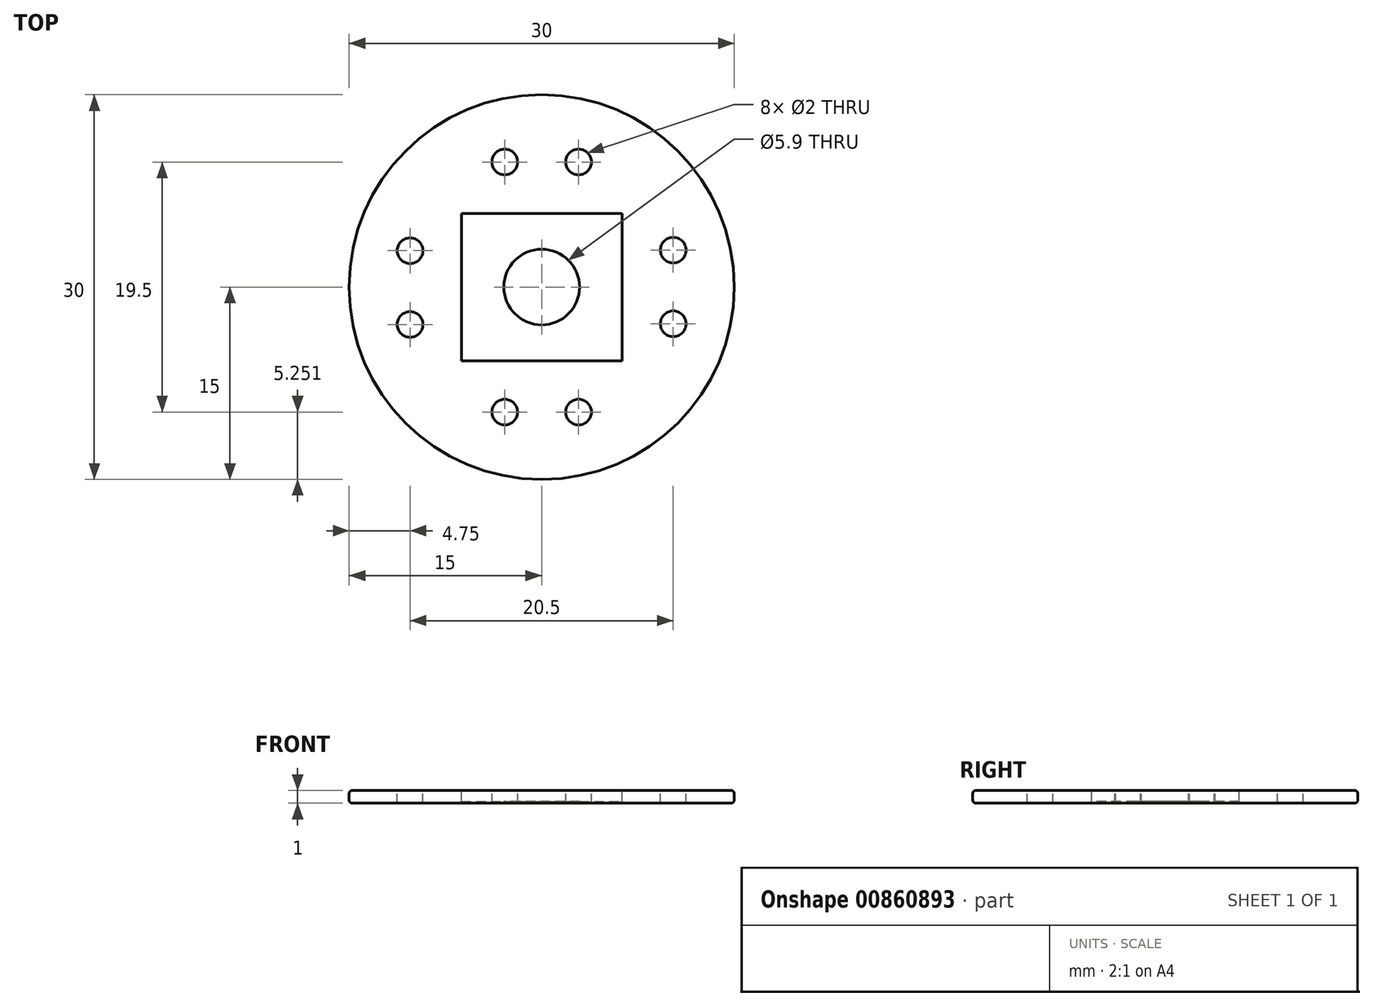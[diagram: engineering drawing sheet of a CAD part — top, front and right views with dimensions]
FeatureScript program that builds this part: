
annotation { "Feature Type Name" : "Feature", "Feature Type Description" : "" }
export const myFeature = defineFeature(function(context is Context, id is Id, definition is map)
    precondition{}
    {
        {
            var Q0;
            Q0=qCreatedBy(makeId("Top.planeOp"),FACE);
            var sketch = newSketch(context, id + "F0", { "sketchPlane" : qUnion([Q0])});
            skCircle(sketch, "E0", {"center": v(0, 0) * mm, "radius": 15 * mm});
            skSolve(sketch);
        }
        {
            var Q0;
            Q0=makeQuery(id+"F0.imprint","IMPRINT",FACE,{"disambiguationData":[TD([[makeQuery(id+"F0.imprint","IMPRINT",EDGE,{"derivedFrom":sQuery(id+"F0.wireOp",EDGE,"E0")}),1.0]])]});
            extrude(context, id + "F1", {"entities" : qUnion([Q0]), "depth" : 1 * mm, "offsetDistance" : 25 * mm});
        }
        {
            var Q0;
            Q0=makeQuery(id+"F1.opExtrude","CAP_FACE",FACE,{"disambiguationData":[OSD([sQuery(id+"F0.wireOp",EDGE,"E0")])],"isStart":false});
            var sketch = newSketch(context, id + "F2", { "sketchPlane" : qUnion([Q0])});
            skLineSegment(sketch, "E1.bottom", {"start": v(-6.25, 5.75) * mm, "end": v(6.25, 5.75) * mm});
            skLineSegment(sketch, "E1.top", {"start": v(-6.25, -5.75) * mm, "end": v(6.25, -5.75) * mm});
            skLineSegment(sketch, "E1.left", {"start": v(-6.25, 5.75) * mm, "end": v(-6.25, -5.75) * mm});
            skLineSegment(sketch, "E1.right", {"start": v(6.25, 5.75) * mm, "end": v(6.25, -5.75) * mm});
            skSolve(sketch);
        }
        {
            var Q0;
            Q0=makeQuery(id+"F2.imprint","IMPRINT",FACE,{"disambiguationData":[TD([[makeQuery(id+"F2.imprint","IMPRINT",EDGE,{"derivedFrom":sQuery(id+"F2.wireOp",EDGE,"E1.bottom")}),-1.0]])]});
            extrude(context, id + "F3", {"entities" : qUnion([Q0]), "operationType" : NewBodyOperationType.REMOVE, "oppositeDirection" : true, "depth" : 0.85 * mm, "offsetDistance" : 25 * mm});
        }
        {
            var Q0;
            Q0=qCreatedBy(makeId("Top.planeOp"),FACE);
            cPlane(context, id + "F4", {"entities" : qUnion([Q0]), "cplaneType" : CPlaneType.OFFSET, "offset" : 0.15 * mm, "width" : 150 * mm, "height" : 150 * mm});
        }
        {
            var Q0;
            Q0=qCreatedBy(id+"F4.planeOp",FACE);
            var sketch = newSketch(context, id + "F5", { "sketchPlane" : qUnion([Q0])});
            skCircle(sketch, "E2", {"center": v(0, 0) * mm, "radius": 2.95 * mm});
            skSolve(sketch);
        }
        {
            var Q0;
            Q0=qSketchRegion(id+"F5",true);
            extrude(context, id + "F6", {"entities" : qUnion([Q0]), "operationType" : NewBodyOperationType.REMOVE, "oppositeDirection" : true, "depth" : 0.15 * mm, "offsetDistance" : 25 * mm});
        }
        {
            var Q0;
            Q0=makeQuery(id+"F1.opExtrude","CAP_EDGE",EDGE,{"disambiguationData":[OSD([sQuery(id+"F0.wireOp",EDGE,"E0")])],"isStart":false});
            var Q1;
            Q1=makeQuery(id+"F1.opExtrude","CAP_EDGE",EDGE,{"disambiguationData":[OSD([sQuery(id+"F0.wireOp",EDGE,"E0")])],"isStart":true});
            var Q2;
            Q2=makeQuery(id+"F1.opExtrude","CAP_EDGE",EDGE,{"disambiguationData":[OSD([sQuery(id+"F0.wireOp",EDGE,"E0")])],"isStart":false});
            fillet(context, id + "F7", {"entities" : qUnion([Q0, Q1, Q2]), "radius" : 0.25 * mm, "tangentPropagation" : true, "allowEdgeOverflow" : false});
        }
        {
            var Q0;
            Q0=makeQuery(id+"F1.opExtrude","CAP_FACE",FACE,{"disambiguationData":[OSD([sQuery(id+"F0.wireOp",EDGE,"E0")])],"isStart":false});
            var sketch = newSketch(context, id + "F8", { "sketchPlane" : qUnion([Q0])});
            skCircle(sketch, "E3", {"center": v(-10.25, 2.83) * mm, "radius": 1 * mm});
            skCircle(sketch, "E4", {"center": v(-10.25, -2.92) * mm, "radius": 1 * mm});
            skLineSegment(sketch, "E5", {"start": v(-2.88, 13.32) * mm, "end": v(-2.87, -11.69) * mm, "construction": true});
            skLineSegment(sketch, "E6", {"start": v(2.87, 13.36) * mm, "end": v(2.88, -11.51) * mm, "construction": true});
            skCircle(sketch, "E7", {"center": v(-2.87, -9.75) * mm, "radius": 1 * mm});
            skCircle(sketch, "E8", {"center": v(2.88, -9.75) * mm, "radius": 1 * mm});
            skLineSegment(sketch, "E9", {"start": v(-17, 2.87) * mm, "end": v(17.76, 2.88) * mm, "construction": true});
            skLineSegment(sketch, "E10", {"start": v(17.76, -2.83) * mm, "end": v(-17.34, -2.92) * mm, "construction": true});
            skCircle(sketch, "E11", {"center": v(10.25, 2.88) * mm, "radius": 1 * mm});
            skCircle(sketch, "E12", {"center": v(10.25, -2.86) * mm, "radius": 1 * mm});
            skCircle(sketch, "E13", {"center": v(-2.88, 9.75) * mm, "radius": 1 * mm});
            skCircle(sketch, "E14", {"center": v(2.87, 9.75) * mm, "radius": 1 * mm});
            skSolve(sketch);
        }
        {
            var Q0;
            Q0=makeQuery(id+"F8.imprint","IMPRINT",FACE,{"disambiguationData":[TD([[makeQuery(id+"F8.imprint","IMPRINT",EDGE,{"derivedFrom":sQuery(id+"F8.wireOp",EDGE,"E3")}),1.0]])]});
            var Q1;
            Q1=makeQuery(id+"F8.imprint","IMPRINT",FACE,{"disambiguationData":[TD([[makeQuery(id+"F8.imprint","IMPRINT",EDGE,{"derivedFrom":sQuery(id+"F8.wireOp",EDGE,"E4")}),1.0]])]});
            var Q2;
            Q2=makeQuery(id+"F8.imprint","IMPRINT",FACE,{"disambiguationData":[TD([[makeQuery(id+"F8.imprint","IMPRINT",EDGE,{"derivedFrom":sQuery(id+"F8.wireOp",EDGE,"E13")}),1.0]])]});
            var Q3;
            Q3=makeQuery(id+"F8.imprint","IMPRINT",FACE,{"disambiguationData":[TD([[makeQuery(id+"F8.imprint","IMPRINT",EDGE,{"derivedFrom":sQuery(id+"F8.wireOp",EDGE,"E14")}),1.0]])]});
            var Q4;
            Q4=makeQuery(id+"F8.imprint","IMPRINT",FACE,{"disambiguationData":[TD([[makeQuery(id+"F8.imprint","IMPRINT",EDGE,{"derivedFrom":sQuery(id+"F8.wireOp",EDGE,"E11")}),1.0]])]});
            var Q5;
            Q5=makeQuery(id+"F8.imprint","IMPRINT",FACE,{"disambiguationData":[TD([[makeQuery(id+"F8.imprint","IMPRINT",EDGE,{"derivedFrom":sQuery(id+"F8.wireOp",EDGE,"E12")}),1.0]])]});
            var Q6;
            Q6=makeQuery(id+"F8.imprint","IMPRINT",FACE,{"disambiguationData":[TD([[makeQuery(id+"F8.imprint","IMPRINT",EDGE,{"derivedFrom":sQuery(id+"F8.wireOp",EDGE,"E8")}),1.0]])]});
            var Q7;
            Q7=makeQuery(id+"F8.imprint","IMPRINT",FACE,{"disambiguationData":[TD([[makeQuery(id+"F8.imprint","IMPRINT",EDGE,{"derivedFrom":sQuery(id+"F8.wireOp",EDGE,"E7")}),1.0]])]});
            var Q8;
            Q8=sQuery(id+"F8.wireOp",EDGE,"E12");
            var Q9;
            Q9=sQuery(id+"F8.wireOp",EDGE,"E8");
            var Q10;
            Q10=sQuery(id+"F8.wireOp",EDGE,"E7");
            var Q11;
            Q11=sQuery(id+"F8.wireOp",EDGE,"E4");
            var Q12;
            Q12=sQuery(id+"F8.wireOp",EDGE,"E3");
            var Q13;
            Q13=sQuery(id+"F8.wireOp",EDGE,"E13");
            var Q14;
            Q14=sQuery(id+"F8.wireOp",EDGE,"E14");
            var Q15;
            Q15=sQuery(id+"F8.wireOp",EDGE,"E11");
            var Q16;
            Q16=makeQuery(id+"F1.opExtrude","SWEPT_BODY",BODY,{"disambiguationData":[OSD([sQuery(id+"F0.wireOp",EDGE,"E0")])]});
            extrude(context, id + "F9", {"entities" : qUnion([Q0, Q1, Q2, Q3, Q4, Q5, Q6, Q7]), "operationType" : NewBodyOperationType.REMOVE, "surfaceEntities" : qUnion([Q8, Q9, Q10, Q11, Q12, Q13, Q14, Q15]), "oppositeDirection" : true, "depth" : 1 * mm, "endBoundEntityBody" : qUnion([Q16]), "offsetDistance" : 25 * mm});
        }
    });
